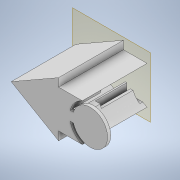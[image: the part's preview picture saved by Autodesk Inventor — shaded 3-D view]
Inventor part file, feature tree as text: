
AUTODESK INVENTOR PART (.ipt)
format: ipt  version: 2022.3 (Build 263350000, 350)  size: 237,056 bytes
history: native  units: mm
features: extrude x5, sketch x5, reference x4, projected_geometry x4, other x2, plane x1
ambient origin geometry x8: Origin, YZ Plane, XZ Plane, XY Plane, X Axis, Y Axis, Z Axis, Center Point
bodies: Solid1 (feature_tree)
feature tree (21):
  plane  "Work Plane1"
  extrude  "Extrusion1"  Depth=2.0mm TaperAngle=0.0deg
  extrude  "Extrusion2"  Depth=0.2mm
  extrude  "Extrusion3"  Depth=1.0mm
  extrude  "Extrusion4"  Depth=17.0mm TaperAngle=0.0deg
  extrude  "Extrusion5"  [1 undecoded]
  sketch  "Sketch1"  dims[d0=41.0mm d1=0.0mm d2=2.0mm d3=0.0mm]
  reference  "Reference1"
  sketch  "Sketch2"  dims[d4=0.2mm d5=0.2mm]
  projected_geometry  "Projected Loop1"
  reference  "Reference2"
  sketch  "Sketch3"  dims[d6=1.0mm d7=1.0mm]
  reference  "Reference3"
  reference  "Reference4"
  projected_geometry  "Projected Loop2"
  sketch  "Sketch4"  dims[d8=37.0mm d9=0.0mm d10=17.0mm d11=0.0mm]
  projected_geometry  "Projected Loop3"
  sketch  "Sketch5"  dims[d12=17.0mm d13=0.0mm]
  projected_geometry  "Projected Loop4"
  other  "v2.0.iam"
  other  "Base:1"
note: 1 required parameter value undecoded (feature->parameter linkage not recoverable at this tier; creation-order binding heuristic only, values carry confidence <= 0.55)
